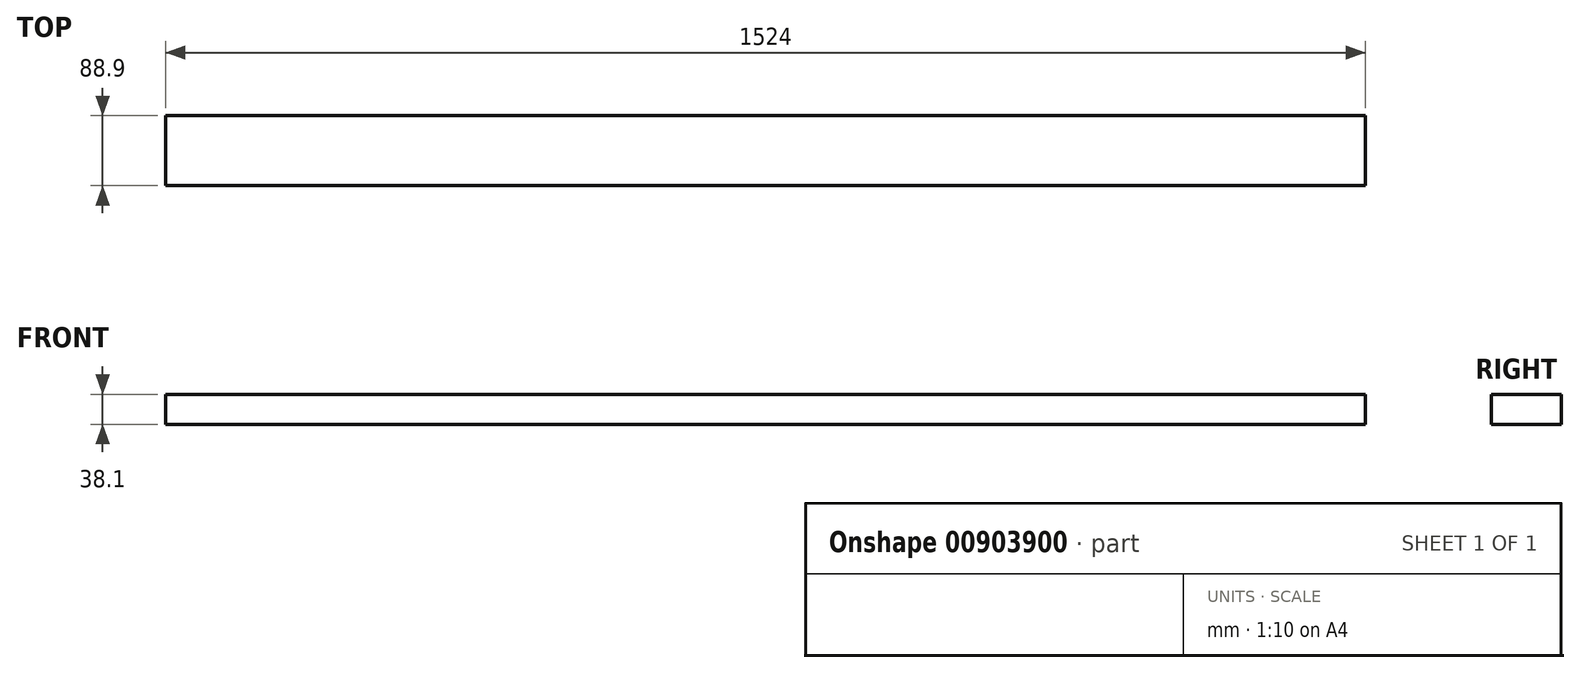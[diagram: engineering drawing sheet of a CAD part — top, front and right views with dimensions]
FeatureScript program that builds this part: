
annotation { "Feature Type Name" : "Feature", "Feature Type Description" : "" }
export const myFeature = defineFeature(function(context is Context, id is Id, definition is map)
    precondition{}
    {
        {
            var Q0;
            Q0=qCreatedBy(makeId("Top.planeOp"),FACE);
            var sketch = newSketch(context, id + "F0", { "sketchPlane" : qUnion([Q0])});
            skLineSegment(sketch, "E0", {"start": v(0, 0) * mm, "end": v(1524, 0) * mm});
            skLineSegment(sketch, "E1", {"start": v(1524, 0) * mm, "end": v(1524, 88.9) * mm});
            skLineSegment(sketch, "E2", {"start": v(1524, 88.9) * mm, "end": v(0, 88.9) * mm});
            skLineSegment(sketch, "E3", {"start": v(0, 88.9) * mm, "end": v(0, 0) * mm});
            skSolve(sketch);
        }
        {
            var Q0;
            Q0=makeQuery(id+"F0.imprint","IMPRINT",FACE,{"disambiguationData":[TD([[makeQuery(id+"F0.imprint","IMPRINT",EDGE,{"derivedFrom":sQuery(id+"F0.wireOp",EDGE,"E0")}),1.0]])]});
            extrude(context, id + "F1", {"entities" : qUnion([Q0]), "depth" : 38.1 * mm, "offsetDistance" : 25.4 * mm});
        }
    });
